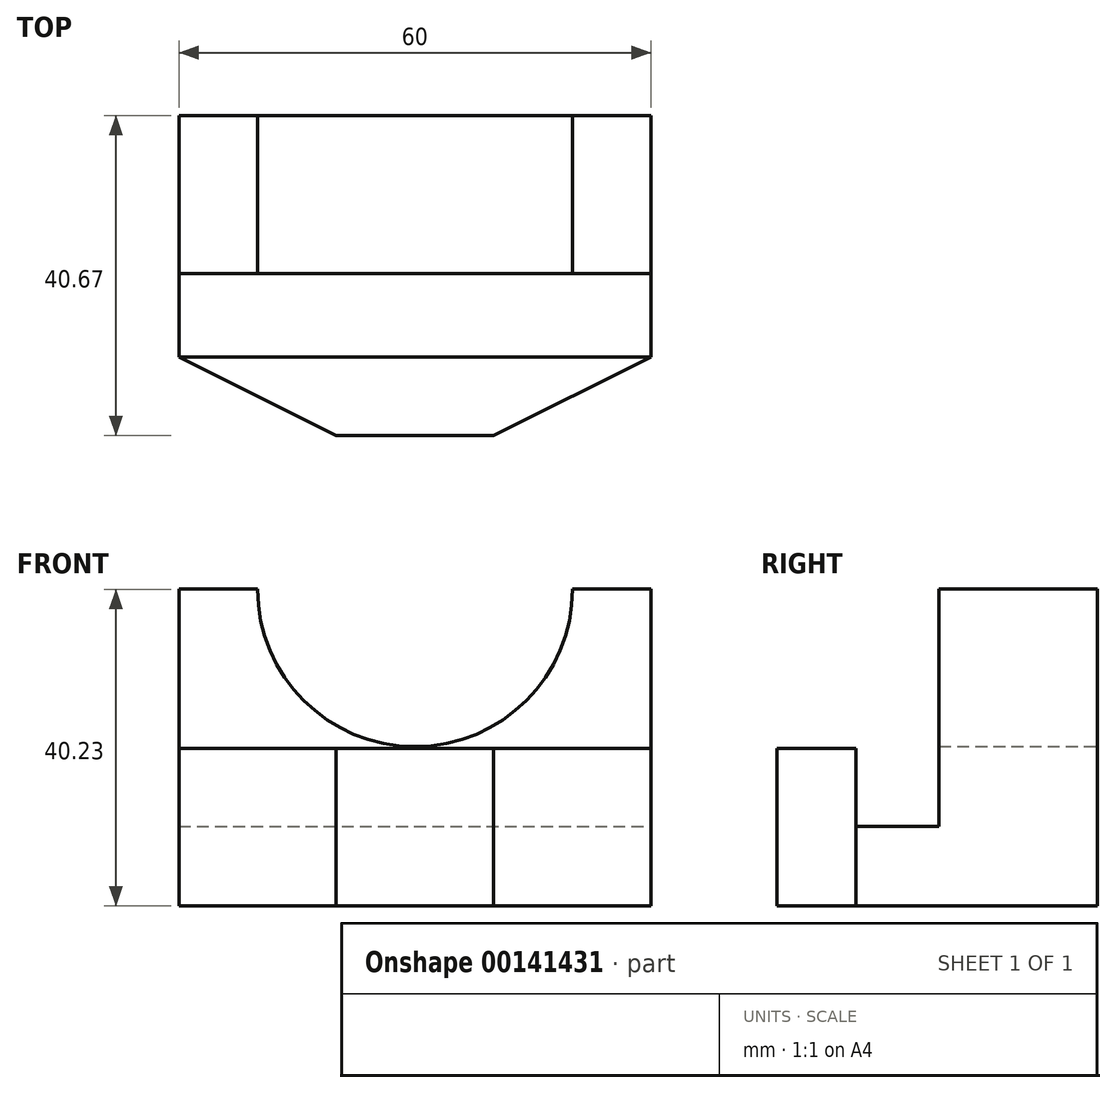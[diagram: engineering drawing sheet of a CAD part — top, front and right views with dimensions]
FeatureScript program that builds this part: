
annotation { "Feature Type Name" : "Feature", "Feature Type Description" : "" }
export const myFeature = defineFeature(function(context is Context, id is Id, definition is map)
    precondition{}
    {
        {
            var Q0;
            Q0=qCreatedBy(makeId("Right.planeOp"),FACE);
            var sketch = newSketch(context, id + "F0", { "sketchPlane" : qUnion([Q0])});
            skLineSegment(sketch, "E0", {"start": v(0, 0) * mm, "end": v(0, 10.1) * mm});
            skLineSegment(sketch, "E1", {"start": v(0, 10.1) * mm, "end": v(10.58, 10.1) * mm});
            skLineSegment(sketch, "E2", {"start": v(10.58, 10.1) * mm, "end": v(10.58, 40.23) * mm});
            skLineSegment(sketch, "E3", {"start": v(10.58, 40.23) * mm, "end": v(30.67, 40.23) * mm});
            skLineSegment(sketch, "E4", {"start": v(30.67, 40.23) * mm, "end": v(30.67, 0) * mm});
            skLineSegment(sketch, "E5", {"start": v(30.67, 0) * mm, "end": v(0, 0) * mm});
            skSolve(sketch);
        }
        {
            var Q0;
            Q0 = qSketchRegion(id + "F0", true);
            extrude(context, id + "F1", {"entities" : qUnion([Q0]), "oppositeDirection" : true, "depth" : 60 * mm});
        }
        {
            var Q0;
            Q0=makeQuery(id+"F1.opExtrude","SWEPT_FACE",FACE,{"disambiguationData":[OSD([sQuery(id+"F0.wireOp",EDGE,"E4")])]});
            var sketch = newSketch(context, id + "F2", { "sketchPlane" : qUnion([Q0])});
            skArc(sketch, "E6", {"start": v(10, 40.23) * mm, "mid": v(30, 20.23) * mm, "end": v(50, 40.23) * mm});
            skLineSegment(sketch, "E7", {"start": v(10, 40.23) * mm, "end": v(50, 40.23) * mm});
            skSolve(sketch);
        }
        {
            var Q0;
            Q0 = qSketchRegion(id + "F2", true);
            extrude(context, id + "F3", {"entities" : qUnion([Q0]), "operationType" : NewBodyOperationType.REMOVE, "endBound" : BoundingType.THROUGH_ALL, "oppositeDirection" : true, "depth" : 25 * mm});
        }
        {
            var Q0;
            Q0=makeQuery(id+"F1.opExtrude","SWEPT_FACE",FACE,{"disambiguationData":[OSD([sQuery(id+"F0.wireOp",EDGE,"E0")])]});
            var sketch = newSketch(context, id + "F4", { "sketchPlane" : qUnion([Q0])});
            skLineSegment(sketch, "E8.bottom", {"start": v(-60, 0) * mm, "end": v(0, 0) * mm});
            skLineSegment(sketch, "E8.top", {"start": v(-60, 20) * mm, "end": v(0, 20) * mm});
            skLineSegment(sketch, "E8.left", {"start": v(-60, 0) * mm, "end": v(-60, 20) * mm});
            skLineSegment(sketch, "E8.right", {"start": v(0, 0) * mm, "end": v(0, 20) * mm});
            skSolve(sketch);
        }
        {
            var Q0;
            Q0 = qSketchRegion(id + "F4", true);
            extrude(context, id + "F5", {"entities" : qUnion([Q0]), "operationType" : NewBodyOperationType.ADD, "depth" : 10 * mm});
        }
        {
            var Q0;
            Q0=makeQuery(id+"F5.opExtrude","SWEPT_FACE",FACE,{"disambiguationData":[OSD([sQuery(id+"F4.wireOp",EDGE,"E8.top")])]});
            var sketch = newSketch(context, id + "F6", { "sketchPlane" : qUnion([Q0])});
            skLineSegment(sketch, "E9", {"start": v(-20, -10) * mm, "end": v(0, 0) * mm});
            skLineSegment(sketch, "E10", {"start": v(0, 0) * mm, "end": v(0, -10) * mm});
            skLineSegment(sketch, "E11", {"start": v(0, -10) * mm, "end": v(-20, -10) * mm});
            skLineSegment(sketch, "E12", {"start": v(-60, 0) * mm, "end": v(-40, -10) * mm});
            skLineSegment(sketch, "E13", {"start": v(-40, -10) * mm, "end": v(-60, -10) * mm});
            skLineSegment(sketch, "E14", {"start": v(-60, -10) * mm, "end": v(-60, 0) * mm});
            skSolve(sketch);
        }
        {
            var Q0;
            Q0 = qSketchRegion(id + "F6", true);
            extrude(context, id + "F7", {"entities" : qUnion([Q0]), "operationType" : NewBodyOperationType.REMOVE, "endBound" : BoundingType.THROUGH_ALL, "oppositeDirection" : true, "depth" : 25 * mm});
        }
    });
